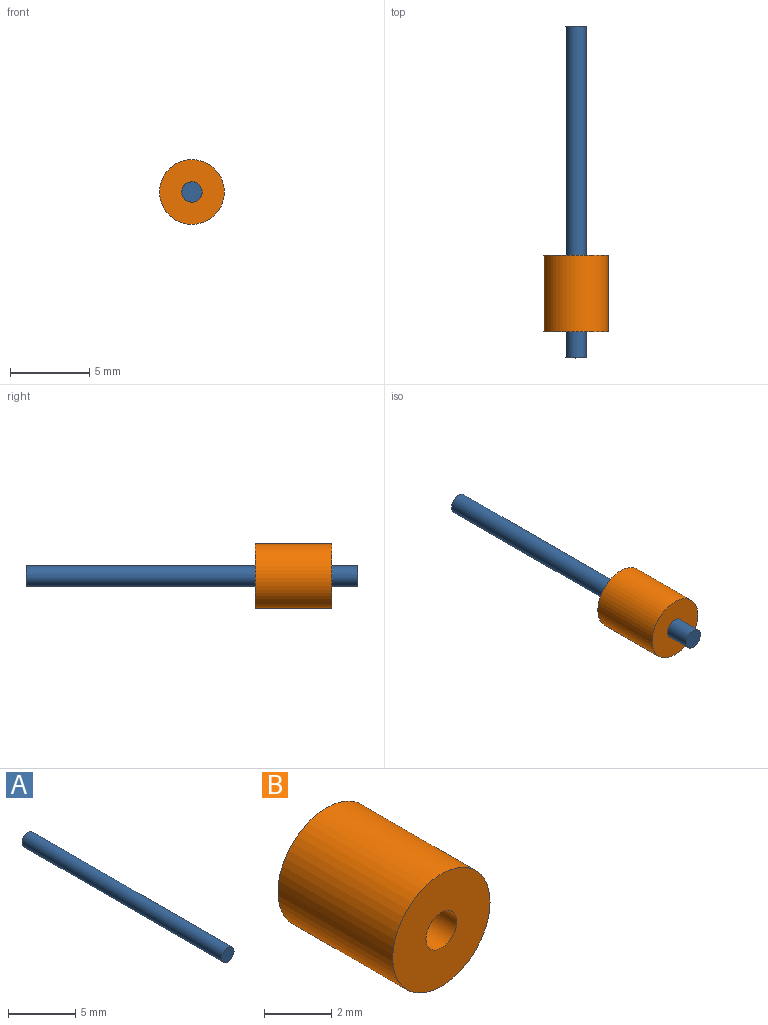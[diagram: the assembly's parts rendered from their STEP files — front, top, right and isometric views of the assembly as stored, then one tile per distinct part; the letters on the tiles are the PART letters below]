
ASSEMBLY  parts=2 mates=1
PART A: 3 faces, bbox 1.3x21x1.3 mm
  f0: cylinder r=0.64mm len=20.96mm, axis (0,1,0), area 83.6mm2, adj f1,f2
  f1: plane 1.27x1.27mm, normal (0,-1,0), area 1.3mm2, adj f0
  f2: plane 1.27x1.27mm, normal (0,1,0), area 1.3mm2, adj f0
PART B: 4 faces, bbox 4.1x4.8x4.1 mm
  f0: cylinder r=2.04mm len=4.83mm, axis (0,1,0), area 62mm2, adj f1,f2
  f1: plane 4.09x4.09mm, normal (0,-1,0), area 11.8mm2, adj f0,f3
  f2: plane 4.09x4.09mm, normal (0,1,0), area 11.8mm2, adj f0,f3
  f3: cylinder r=0.65mm len=4.83mm, axis (0,-1,0), area 19.6mm2, adj f1,f2
PLACE A t=(-8.86,3.75,-2.42)mm
PLACE B t=(-8.86,-10.73,-2.42)mm
MATE fastened B.f0 <-> A.f0  axis (0,-1,0) through (-8.86,-15.55,-2.42)mm
